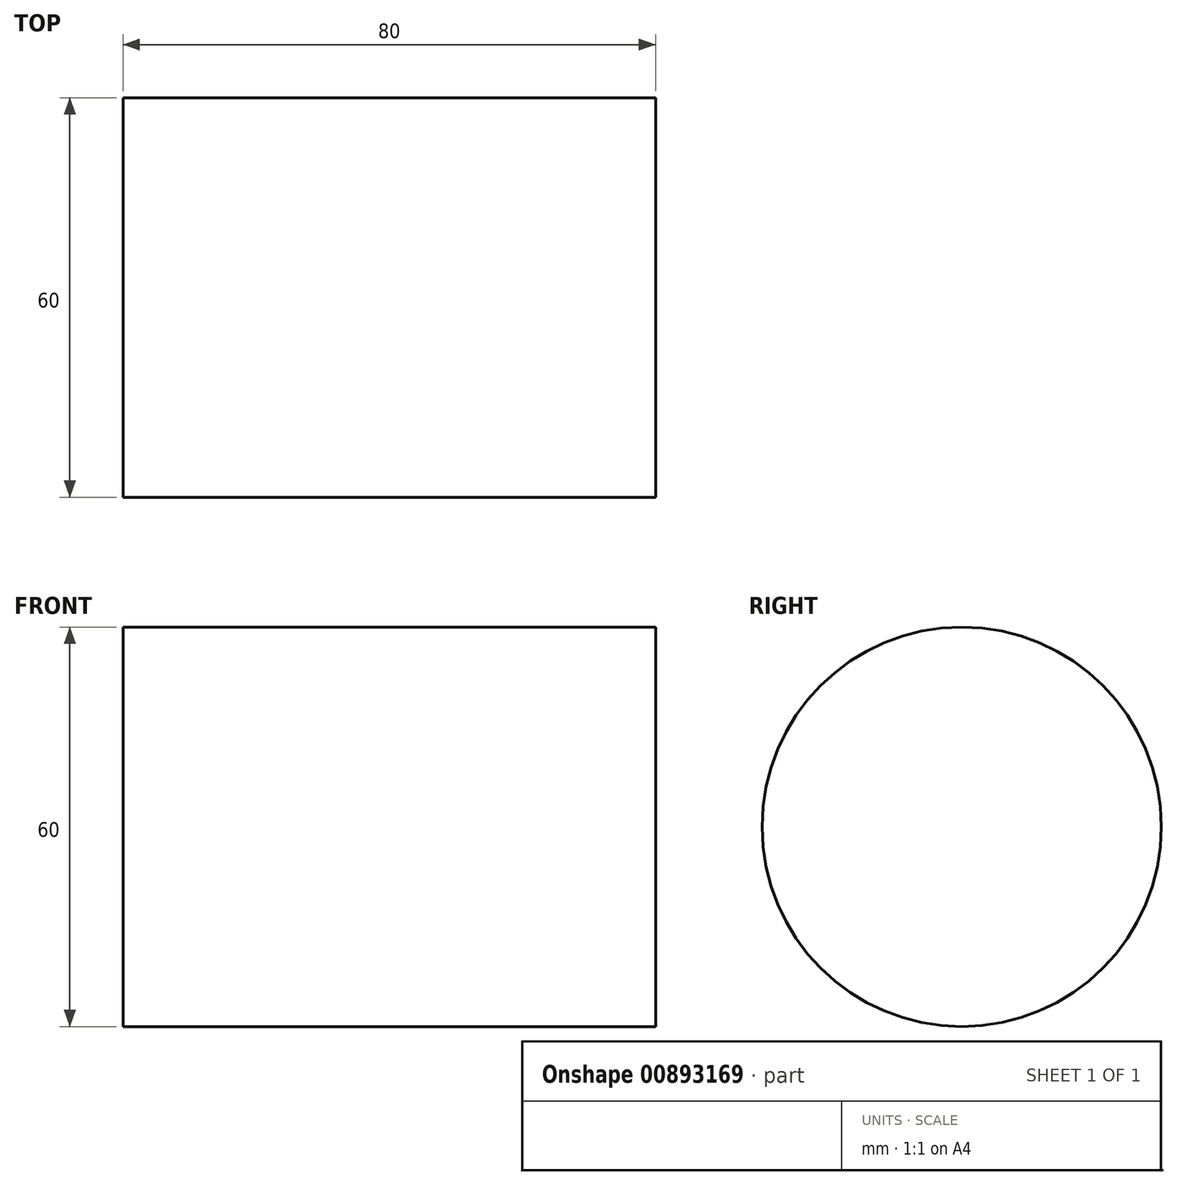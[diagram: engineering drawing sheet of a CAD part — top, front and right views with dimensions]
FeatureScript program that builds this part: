
annotation { "Feature Type Name" : "Feature", "Feature Type Description" : "" }
export const myFeature = defineFeature(function(context is Context, id is Id, definition is map)
    precondition{}
    {
        {
            var Q0;
            Q0=qCreatedBy(makeId("Front.planeOp"),FACE);
            var sketch = newSketch(context, id + "F0", { "sketchPlane" : qUnion([Q0])});
            skLineSegment(sketch, "E0.bottom", {"start": v(40, -30) * mm, "end": v(-40, -30) * mm});
            skLineSegment(sketch, "E0.top", {"start": v(40, 30) * mm, "end": v(-40, 30) * mm});
            skLineSegment(sketch, "E0.left", {"start": v(40, -30) * mm, "end": v(40, 30) * mm});
            skLineSegment(sketch, "E0.right", {"start": v(-40, -30) * mm, "end": v(-40, 30) * mm});
            skPoint(sketch, "E0.middle", {"position": v(0, 0) * mm});
            skLineSegment(sketch, "E1", {"start": v(-40, 10) * mm, "end": v(-25, 10) * mm});
            skLineSegment(sketch, "E2", {"start": v(-25, 10) * mm, "end": v(-25, 0) * mm});
            skLineSegment(sketch, "E3", {"start": v(-25, 0) * mm, "end": v(-40, 0) * mm});
            skLineSegment(sketch, "E4", {"start": v(-25, 0) * mm, "end": v(0, 0) * mm});
            skLineSegment(sketch, "E5", {"start": v(0, 0) * mm, "end": v(40, 0) * mm});
            skSolve(sketch);
        }
        {
            var Q0;
            {var subQ2=sQuery(id+"F0.wireOp",EDGE,"E0.bottom");Q0=makeQuery(id+"F0.imprint","IMPRINT",FACE,{"disambiguationData":[TD([[makeQuery(id+"F0.imprint","IMPRINT",EDGE,{"derivedFrom":subQ2}),-1.0]])]});}
            var Q1;
            Q1=sQuery(id+"F0.wireOp",EDGE,"E3");
            revolve(context, id + "F1", {"surfaceOperationType" : NewSurfaceOperationType.NEW, "entities" : qUnion([Q0]), "axis" : qUnion([Q1]), "revolveType" : RevolveType.FULL});
        }
    });
